# Revit family: FU_Table_Sandler_Nume 9-2FH
name_source: partatom
category: Furniture
units: mm (PartAtom-declared; Revit-internal decimal feet)

## family parameters
Always vertical = Yes
Cut with Voids When Loaded = No
OmniClass Number = 23.40.20.00
OmniClass Title = General Furniture and Specialties
Room Calculation Point = No
Shared = No
Work Plane-Based = No

## types (2) — shared parameters
Depth = 400 mm  [stored 1.31234 ft]
Description = Fixed height side table, with wood top and steel base.
Height = 660 mm
Manufacturer = Sandler
Model = Nume 9.2FH
URL = https://www.sandlerseating.com
Width = 400 mm  [stored 1.31234 ft]
zero-valued in all types: Default Elevation

## per-type parameters (varying)
| type | Base Finish | Top Finish | Top Type |
| NUME 9.2FH HPL/Fenix Top | Epoxy - M1_Aluminum | HPL - Solid - Black | Nume_HPL_Top : Nume HPL 400x12mm |
| Nume 9.2FH Wood/Laminate Top | Epoxy - M1_B00 - Black | Wood - Oak - Walnut | Nume_Wood_Top : Nume Wood 400x19mm |

note: [stored X ft] marks values corroborated as IEEE doubles in the binary element streams (Revit-internal decimal feet)

## geometry (parser evidence)
native form markers: Sweep x9
no freeform markers — native parametric forms only
